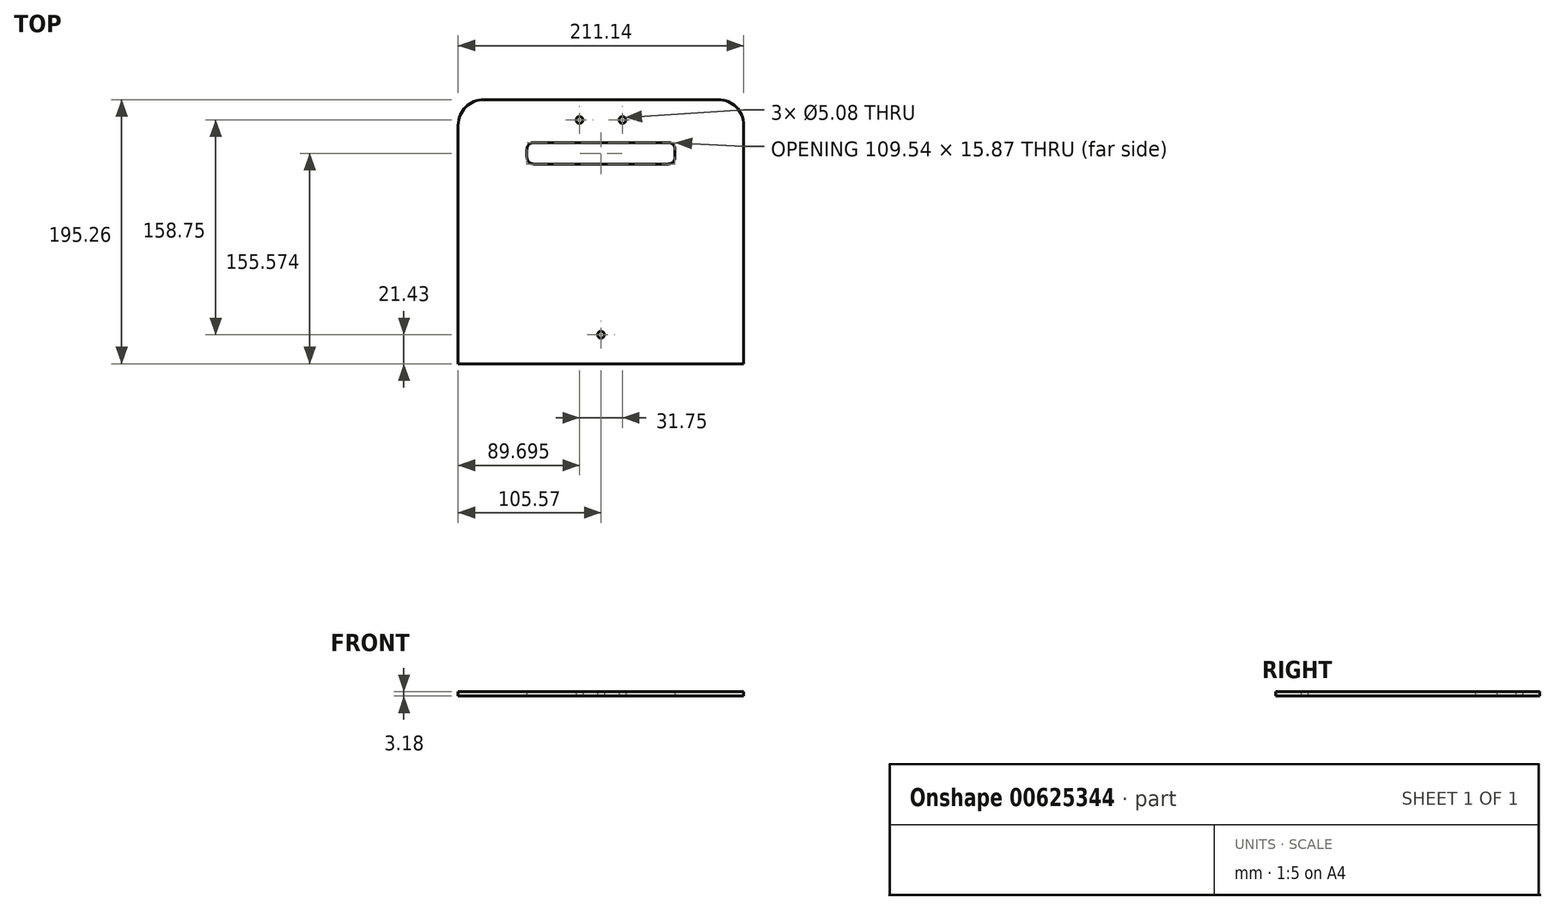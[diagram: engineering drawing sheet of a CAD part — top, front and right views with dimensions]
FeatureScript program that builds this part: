
annotation { "Feature Type Name" : "Feature", "Feature Type Description" : "" }
export const myFeature = defineFeature(function(context is Context, id is Id, definition is map)
    precondition{}
    {
        {
            var Q0;
            Q0=qCreatedBy(makeId("Top.planeOp"),FACE);
            var sketch = newSketch(context, id + "F0", { "sketchPlane" : qUnion([Q0])});
            skLineSegment(sketch, "E0.bottom", {"start": v(-105.57, 97.63) * mm, "end": v(105.57, 97.63) * mm});
            skLineSegment(sketch, "E0.top", {"start": v(-105.57, -97.63) * mm, "end": v(105.57, -97.63) * mm});
            skLineSegment(sketch, "E0.left", {"start": v(-105.57, 97.63) * mm, "end": v(-105.57, -97.63) * mm});
            skLineSegment(sketch, "E0.right", {"start": v(105.57, 97.63) * mm, "end": v(105.57, -97.63) * mm});
            skPoint(sketch, "E0.middle", {"position": v(0, 0) * mm});
            skLineSegment(sketch, "E1", {"start": v(-15.88, 82.55) * mm, "end": v(15.88, 82.55) * mm, "construction": true});
            skLineSegment(sketch, "E2", {"start": v(0, 82.55) * mm, "end": v(0, 0) * mm, "construction": true});
            skCircle(sketch, "E3", {"center": v(-15.88, 82.55) * mm, "radius": 2.54 * mm});
            skCircle(sketch, "E4", {"center": v(15.88, 82.55) * mm, "radius": 2.54 * mm});
            skCircle(sketch, "E5", {"center": v(0, -76.2) * mm, "radius": 2.54 * mm});
            skLineSegment(sketch, "E6.bottom", {"start": v(-54.77, 65.88) * mm, "end": v(54.77, 65.88) * mm});
            skLineSegment(sketch, "E6.top", {"start": v(-54.77, 50) * mm, "end": v(54.77, 50) * mm});
            skLineSegment(sketch, "E6.left", {"start": v(-54.77, 65.88) * mm, "end": v(-54.77, 50) * mm});
            skLineSegment(sketch, "E6.right", {"start": v(54.77, 65.88) * mm, "end": v(54.77, 50) * mm});
            skPoint(sketch, "E6.middle", {"position": v(0, 57.94) * mm});
            skSolve(sketch);
        }
        {
            var Q0;
            Q0 = qSketchRegion(id + "F0", true);
            extrude(context, id + "F1", {"entities" : qUnion([Q0]), "depth" : 3.17 * mm, "offsetDistance" : 25.4 * mm});
        }
        {
            var Q0;
            Q0=makeQuery(id+"F1.opExtrude","SWEPT_EDGE",EDGE,{"disambiguationData":[OSD([sQuery(id+"F0.wireOp",EDGE,"E0.bottom"),sQuery(id+"F0.wireOp",EDGE,"E0.left")])]});
            var Q1;
            Q1=makeQuery(id+"F1.opExtrude","SWEPT_EDGE",EDGE,{"disambiguationData":[OSD([sQuery(id+"F0.wireOp",EDGE,"E0.bottom"),sQuery(id+"F0.wireOp",EDGE,"E0.right")])]});
            fillet(context, id + "F2", {"entities" : qUnion([Q0, Q1]), "radius" : 19.05 * mm, "tangentPropagation" : true, "allowEdgeOverflow" : false});
        }
        {
            var Q0;
            Q0=makeQuery(id+"F1.opExtrude","SWEPT_EDGE",EDGE,{"disambiguationData":[OSD([sQuery(id+"F0.wireOp",EDGE,"E6.top"),sQuery(id+"F0.wireOp",EDGE,"E6.left")])]});
            var Q1;
            Q1=makeQuery(id+"F1.opExtrude","SWEPT_EDGE",EDGE,{"disambiguationData":[OSD([sQuery(id+"F0.wireOp",EDGE,"E6.bottom"),sQuery(id+"F0.wireOp",EDGE,"E6.left")])]});
            var Q2;
            Q2=makeQuery(id+"F1.opExtrude","SWEPT_EDGE",EDGE,{"disambiguationData":[OSD([sQuery(id+"F0.wireOp",EDGE,"E6.top"),sQuery(id+"F0.wireOp",EDGE,"E6.right")])]});
            var Q3;
            Q3=makeQuery(id+"F1.opExtrude","SWEPT_EDGE",EDGE,{"disambiguationData":[OSD([sQuery(id+"F0.wireOp",EDGE,"E6.bottom"),sQuery(id+"F0.wireOp",EDGE,"E6.right")])]});
            fillet(context, id + "F3", {"entities" : qUnion([Q0, Q1, Q2, Q3]), "radius" : 5.08 * mm, "tangentPropagation" : true, "allowEdgeOverflow" : false});
        }
    });
